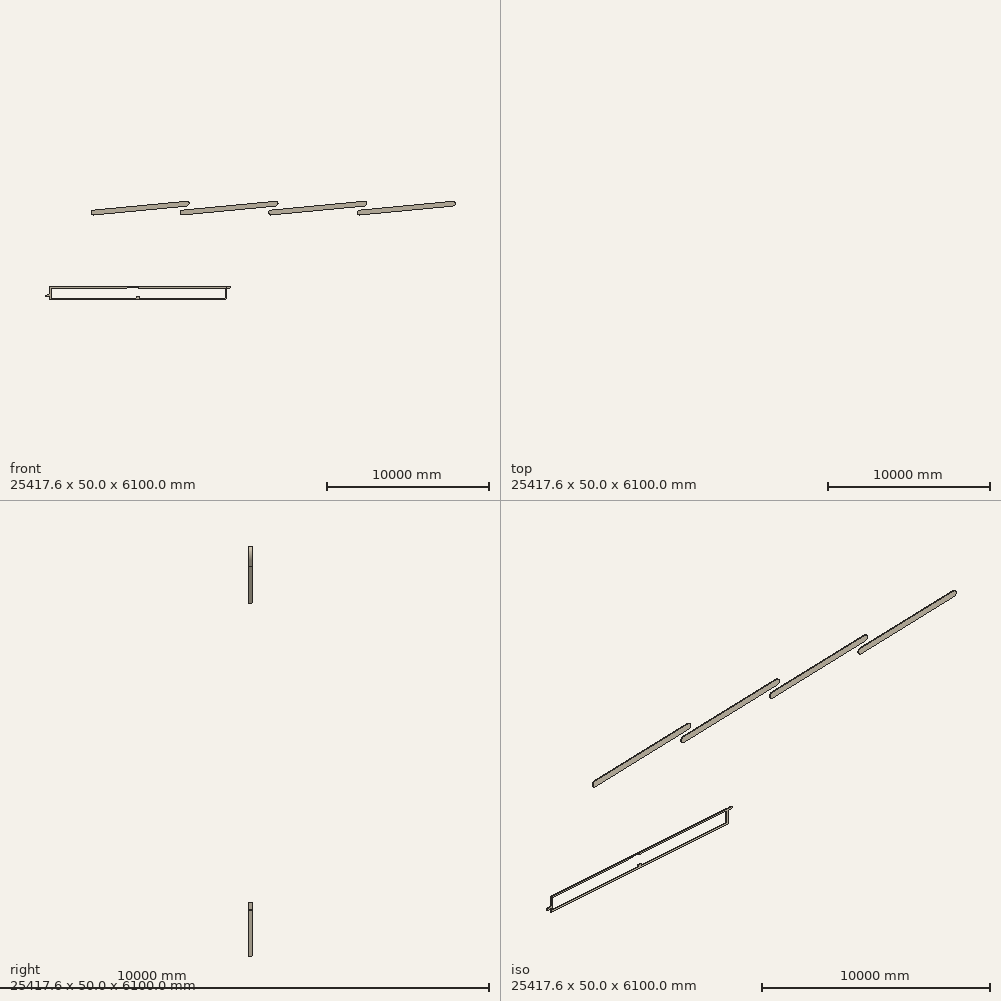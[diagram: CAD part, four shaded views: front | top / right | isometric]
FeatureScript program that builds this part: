
annotation { "Feature Type Name" : "Feature", "Feature Type Description" : "" }
export const myFeature = defineFeature(function(context is Context, id is Id, definition is map)
    precondition{}
    {
        {
            var Q0;
            Q0=qCreatedBy(makeId("Front.planeOp"),FACE);
            var sketch = newSketch(context, id + "F0", { "sketchPlane" : qUnion([Q0])});
            skCircle(sketch, "E0", {"center": v(0, 0) * mm, "radius": 150 * mm});
            skCircle(sketch, "E1", {"center": v(5773.86, 550) * mm, "radius": 150 * mm});
            skLineSegment(sketch, "E2", {"start": v(-14.22, 149.32) * mm, "end": v(5759.64, 699.32) * mm});
            skLineSegment(sketch, "E3", {"start": v(5759.64, 699.32) * mm, "end": v(5788.09, 400.68) * mm});
            skLineSegment(sketch, "E4", {"start": v(5788.09, 400.68) * mm, "end": v(14.22, -149.32) * mm});
            skLineSegment(sketch, "E5", {"start": v(14.22, -149.32) * mm, "end": v(-14.22, 149.32) * mm});
            skCircle(sketch, "E6", {"center": v(5500, 0) * mm, "radius": 150 * mm});
            skCircle(sketch, "E7", {"center": v(11273.86, 550) * mm, "radius": 150 * mm});
            skLineSegment(sketch, "E8", {"start": v(5485.78, 149.32) * mm, "end": v(11259.64, 699.32) * mm});
            skLineSegment(sketch, "E9", {"start": v(11288.09, 400.68) * mm, "end": v(5514.22, -149.32) * mm});
            skCircle(sketch, "E10", {"center": v(11000, 0) * mm, "radius": 150 * mm});
            skCircle(sketch, "E11", {"center": v(16773.86, 550) * mm, "radius": 150 * mm});
            skLineSegment(sketch, "E12", {"start": v(10985.78, 149.32) * mm, "end": v(16759.64, 699.32) * mm});
            skLineSegment(sketch, "E13", {"start": v(16759.64, 699.32) * mm, "end": v(16788.09, 400.68) * mm});
            skLineSegment(sketch, "E14", {"start": v(16788.09, 400.68) * mm, "end": v(11014.22, -149.32) * mm});
            skLineSegment(sketch, "E15", {"start": v(11014.22, -149.32) * mm, "end": v(10985.78, 149.32) * mm});
            skCircle(sketch, "E16", {"center": v(16500, 0) * mm, "radius": 150 * mm});
            skCircle(sketch, "E17", {"center": v(22273.86, 550) * mm, "radius": 150 * mm});
            skLineSegment(sketch, "E18", {"start": v(16485.78, 149.32) * mm, "end": v(22259.64, 699.32) * mm});
            skLineSegment(sketch, "E19", {"start": v(22288.09, 400.68) * mm, "end": v(16514.22, -149.32) * mm});
            skLineSegment(sketch, "E20", {"start": v(0, 0) * mm, "end": v(5773.86, 550) * mm});
            skLineSegment(sketch, "E21", {"start": v(0, 0) * mm, "end": v(6000, 0) * mm});
            skLineSegment(sketch, "E22.bottom", {"start": v(2750, -4600) * mm, "end": v(-2750, -4600) * mm});
            skLineSegment(sketch, "E22.top", {"start": v(2750, -5400) * mm, "end": v(-2750, -5400) * mm});
            skLineSegment(sketch, "E22.left", {"start": v(2750, -4600) * mm, "end": v(2750, -5400) * mm});
            skLineSegment(sketch, "E22.right", {"start": v(-2750, -4600) * mm, "end": v(-2750, -5400) * mm});
            skPoint(sketch, "E22.middle", {"position": v(0, -5000) * mm});
            skLineSegment(sketch, "E23.bottom", {"start": v(2650, -4700) * mm, "end": v(-2650, -4700) * mm});
            skLineSegment(sketch, "E23.top", {"start": v(2650, -5300) * mm, "end": v(-2650, -5300) * mm});
            skLineSegment(sketch, "E23.left", {"start": v(2650, -4700) * mm, "end": v(2650, -5300) * mm});
            skLineSegment(sketch, "E23.right", {"start": v(-2650, -4700) * mm, "end": v(-2650, -5300) * mm});
            skLineSegment(sketch, "E24", {"start": v(-2993.72, -5120.38) * mm, "end": v(2983.45, -4597.45) * mm});
            skLineSegment(sketch, "E25", {"start": v(2983.45, -4597.45) * mm, "end": v(2992.17, -4697.07) * mm});
            skLineSegment(sketch, "E26", {"start": v(2992.17, -4697.07) * mm, "end": v(-2985, -5220) * mm});
            skLineSegment(sketch, "E27", {"start": v(-2985, -5220) * mm, "end": v(-2993.72, -5120.38) * mm});
            skLineSegment(sketch, "E28.bottom", {"start": v(8250, -4600) * mm, "end": v(2750, -4600) * mm});
            skLineSegment(sketch, "E28.top", {"start": v(8250, -5400) * mm, "end": v(2750, -5400) * mm});
            skLineSegment(sketch, "E28.left", {"start": v(8250, -4600) * mm, "end": v(8250, -5400) * mm});
            skPoint(sketch, "E28.middle", {"position": v(5500, -5000) * mm});
            skLineSegment(sketch, "E29.bottom", {"start": v(8150, -4700) * mm, "end": v(2850, -4700) * mm});
            skLineSegment(sketch, "E29.top", {"start": v(8150, -5300) * mm, "end": v(2850, -5300) * mm});
            skLineSegment(sketch, "E29.left", {"start": v(8150, -4700) * mm, "end": v(8150, -5300) * mm});
            skLineSegment(sketch, "E29.right", {"start": v(2850, -4700) * mm, "end": v(2850, -5300) * mm});
            skLineSegment(sketch, "E30", {"start": v(2506.28, -5120.38) * mm, "end": v(8483.45, -4597.45) * mm});
            skLineSegment(sketch, "E31", {"start": v(8483.45, -4597.45) * mm, "end": v(8492.17, -4697.07) * mm});
            skLineSegment(sketch, "E32", {"start": v(8492.17, -4697.07) * mm, "end": v(2515, -5220) * mm});
            skLineSegment(sketch, "E33", {"start": v(2515, -5220) * mm, "end": v(2506.28, -5120.38) * mm});
            skSolve(sketch);
        }
        {
            var Q0;
            Q0 = qSketchRegion(id + "F0", true);
            extrude(context, id + "F1", {"entities" : qUnion([Q0]), "depth" : 50 * mm});
        }
    });
